# Revit family: Toilet_Partition-Bobrick-B1038-Ceiling_Hung (3)
name_source: partatom
category: Specialty Equipment
revit_build: Autodesk Revit 2014 (Build: 20130308_1515(x64)
units: mm (PartAtom-declared; Revit-internal decimal feet)

## types (1)
- B-1038
    Assembly Code = C1030200
    Description = Laminated Plastic Partitions and Screens with Stainless Steel Edges
    Door Panel = Yes
    DoorPanel Width = 24"
    Inswing = Yes
    Inswing Value = 24"
    Inswing Visibility = Yes
    Left Stile Value = 4"
    Left Stile Visible = Yes
    Left Stile Width = 4"
    Manufacturer = Bobrick Washroom Equipment, Inc.
    Model = B1038 TrimLineSeries Ceiling-Hung
    Outswing = No
    Outswing Value = 25"
    Panel = No
    Panel Value = 24"
    Partition Material = Laminated Plastic - Bobrick - Designer White
    Right Stile Value = 4"
    Right Stile Visible = Yes
    Right Stile Width = 4"
    URL = http://www.bobrick.com
    Width Value = 24"

## geometry (parser evidence)
native form markers: Blend x12, Sweep x1
no freeform markers — native parametric forms only
